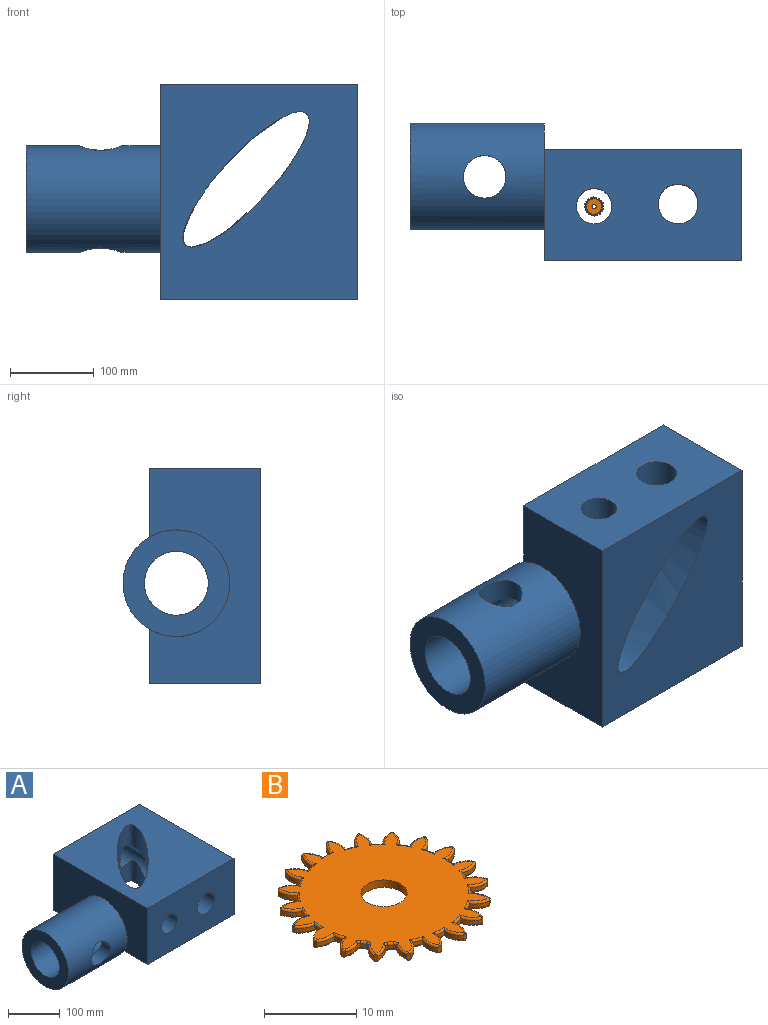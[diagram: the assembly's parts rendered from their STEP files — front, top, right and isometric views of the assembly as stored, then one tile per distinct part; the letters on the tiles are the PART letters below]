
ASSEMBLY  parts=2 mates=1
PART A: 19 faces, bbox 395.5x256.8x164.2 mm
  f0: plane 235.5x116.38mm, normal (0,0,-1), area 22235.5mm2, adj f2,f3,f5,f11,f12,f15,f16
  f1: cylinder r=21.17mm len=150.34mm, axis (0,-1,0), area 14829.1mm2, adj f2,f11,f15
  f2: plane 235.5x132.59mm, normal (0,1,0), area 28054mm2, adj f0,f1,f3,f5,f6,f8
  f3: plane 256.85x132.59mm, normal (-1,0,0), area 23850.9mm2, adj f0,f2,f4,f6,f7,f13
  f4: plane 235.5x132.59mm, normal (0,-1,0), area 28054mm2, adj f3,f5,f6,f7,f8,f10
  f5: plane 256.85x132.59mm, normal (1,0,0), area 29671mm2, adj f0,f2,f4,f6,f7,f16
  f6: plane 256.85x235.5mm, normal (0,0,1), area 50558.2mm2, adj f2,f3,f4,f5,f11
  f7: plane 235.5x98.69mm, normal (0,0,-1), area 21570.9mm2, adj f3,f4,f5,f11,f12,f15,f16
  f8: cylinder r=23.69mm len=256.85mm, axis (0,-1,0), area 26763.2mm2, adj f2,f4,f9,f11,f16
  f9: cylinder r=23.69mm len=12.34mm, axis (0,-1,0), area 49.3mm2, adj f8,f11,f16
  f10: cylinder r=21.17mm len=83.03mm, axis (0,-1,0), area 9437.5mm2, adj f4,f11
  f11: extruded ~161.25x149.84mm, area 41740.2mm2, adj f0,f1,f6,f7,f8,f9,f10,f15
  f12: plane 109.85x31.64mm, normal (1,0,0), area 2287.2mm2, adj f0,f7,f13,f15
  f13: cylinder r=63.5mm len=160.02mm, axis (1,0,0), area 59704.6mm2, adj f3,f12,f14,f17,f18
  f14: plane 127x127mm, normal (-1,0,0), area 8107.3mm2, adj f13,f15
  f15: cylinder r=38.1mm len=235.28mm, axis (-1,0,0), area 42652.1mm2, adj f0,f1,f7,f11,f12,f14,f17,f18
  f16: cylinder r=38.1mm len=157.14mm, axis (-1,0,0), area 18968.1mm2, adj f0,f5,f7,f8,f9,f11
  f17: cylinder r=25.4mm len=50.8mm, axis (0,-1,0), area 4383.1mm2, adj f13,f15
  f18: cylinder r=25.4mm len=50.8mm, axis (0,-1,0), area 4382.4mm2, adj f13,f15
PART B: 214 faces, bbox 23.5x23.5x1 mm
  f0: cylinder r=2.61mm len=2.18mm, axis (0,0,-1), area 1.2mm2, adj f1,f79,f96,f200
  f1: cylinder r=9.41mm len=1.14mm, axis (0,0,-1), area 0.6mm2, adj f0,f2,f95,f201
  f2: cylinder r=2.61mm len=1.71mm, axis (0,0,-1), area 1.2mm2, adj f1,f3,f94,f203
  f3: plane 0.97x0.41mm, normal (-0.38,0.92,0), area 0.4mm2, adj f2,f4,f93,f94,f203,f205
  f4: cylinder r=2.61mm len=2.23mm, axis (0,0,-1), area 1.2mm2, adj f3,f5,f93,f205
  f5: cylinder r=9.41mm len=1mm, axis (0,0,-1), area 0.6mm2, adj f4,f6,f92,f207
  f6: cylinder r=2.61mm len=1.89mm, axis (0,0,-1), area 1.2mm2, adj f5,f7,f91,f209
  f7: plane 0.97x0.34mm, normal (-0.65,0.76,0), area 0.4mm2, adj f6,f8,f90,f91,f209,f211
  f8: cylinder r=2.61mm len=2.06mm, axis (0,0,-1), area 1.2mm2, adj f7,f9,f90,f211
  f9: cylinder r=9.41mm len=0.89mm, axis (0,0,-1), area 0.6mm2, adj f8,f10,f89,f213
  f10: cylinder r=2.61mm len=2.17mm, axis (0,0,-1), area 1.2mm2, adj f9,f11,f88,f212
  f11: plane 0.97x0.38mm, normal (-0.85,0.52,0), area 0.4mm2, adj f10,f12,f87,f88,f210,f212
  f12: cylinder r=2.61mm len=1.68mm, axis (0,0,-1), area 1.2mm2, adj f11,f13,f87,f210
  f13: cylinder r=9.41mm len=1.08mm, axis (0,0,-1), area 0.6mm2, adj f12,f14,f86,f208
  f14: cylinder r=2.61mm len=2.23mm, axis (0,0,-1), area 1.2mm2, adj f13,f15,f85,f206
  f15: plane 0.97x0.43mm, normal (-0.97,0.23,0), area 0.4mm2, adj f14,f16,f84,f85,f204,f206
  f16: cylinder r=2.61mm len=1.92mm, axis (0,0,-1), area 1.2mm2, adj f15,f17,f84,f204
  f17: cylinder r=9.41mm len=1.17mm, axis (0,0,-1), area 0.6mm2, adj f16,f18,f83,f202
  f18: cylinder r=2.61mm len=2.32mm, axis (0,0,-1), area 2.3mm2, adj f17,f19,f81,f82,f83,f169,f202
  f19: plane 0.75x0.44mm, normal (-1,-0.08,0), area 0.3mm2, adj f18,f20,f82,f169,f192
  f20: cylinder r=2.61mm len=2.18mm, axis (0,0,-1), area 1.2mm2, adj f19,f21,f173,f192
  f21: cylinder r=9.41mm len=1.14mm, axis (0,0,-1), area 0.6mm2, adj f20,f22,f176,f195
  f22: cylinder r=2.61mm len=1.71mm, axis (0,0,-1), area 1.2mm2, adj f21,f23,f180,f197
  f23: plane 0.73x0.41mm, normal (-0.92,-0.38,0), area 0.3mm2, adj f22,f24,f183,f197,f198
  f24: cylinder r=2.61mm len=2.02mm, axis (0,0,-1), area 1mm2, adj f23,f186,f193,f198
  f25: cylinder r=9.41mm len=0.59mm, axis (0,0,-1), area 0.3mm2, adj f187,f188,f193,f194
  f26: cylinder r=2.61mm len=1.76mm, axis (0,0,-1), area 1mm2, adj f27,f181,f188,f189
  f27: plane 0.97x0.34mm, normal (-0.76,-0.65,0), area 0.4mm2, adj f26,f28,f177,f181,f185,f189
  f28: cylinder r=2.61mm len=1.89mm, axis (0,0,-1), area 1mm2, adj f27,f177,f178,f185
  f29: cylinder r=9.41mm len=0.52mm, axis (0,0,-1), area 0.3mm2, adj f170,f171,f178,f179
  f30: cylinder r=2.61mm len=1.98mm, axis (0,0,-1), area 1mm2, adj f31,f165,f171,f172
  f31: plane 0.97x0.38mm, normal (-0.52,-0.85,0), area 0.4mm2, adj f30,f32,f163,f165,f168,f172
  f32: cylinder r=2.61mm len=1.68mm, axis (0,0,-1), area 1.2mm2, adj f31,f33,f163,f168
  f33: cylinder r=9.41mm len=1.08mm, axis (0,0,-1), area 0.6mm2, adj f32,f34,f161,f166
  f34: cylinder r=2.61mm len=2.23mm, axis (0,0,-1), area 1.2mm2, adj f33,f35,f159,f164
  f35: plane 0.97x0.43mm, normal (-0.23,-0.97,0), area 0.4mm2, adj f34,f36,f157,f159,f162,f164
  f36: cylinder r=2.61mm len=1.92mm, axis (0,0,-1), area 1.2mm2, adj f35,f37,f157,f162
  f37: cylinder r=9.41mm len=1.17mm, axis (0,0,-1), area 0.6mm2, adj f36,f38,f155,f160
  f38: cylinder r=2.61mm len=2.07mm, axis (0,0,-1), area 1.2mm2, adj f37,f39,f153,f158
  f39: plane 0.97x0.44mm, normal (0.08,-1,0), area 0.4mm2, adj f38,f40,f151,f153,f156,f158
  f40: cylinder r=2.61mm len=2.18mm, axis (0,0,-1), area 1.2mm2, adj f39,f41,f151,f156
  f41: cylinder r=9.41mm len=1.14mm, axis (0,0,-1), area 0.6mm2, adj f40,f42,f149,f154
  f42: cylinder r=2.61mm len=1.71mm, axis (0,0,-1), area 1.2mm2, adj f41,f43,f147,f152
  f43: plane 0.97x0.41mm, normal (0.38,-0.92,0), area 0.4mm2, adj f42,f44,f145,f147,f150,f152
  f44: cylinder r=2.61mm len=2.23mm, axis (0,0,-1), area 1.2mm2, adj f43,f45,f145,f150
  f45: cylinder r=9.41mm len=1mm, axis (0,0,-1), area 0.6mm2, adj f44,f46,f143,f148
  f46: cylinder r=2.61mm len=1.89mm, axis (0,0,-1), area 1.2mm2, adj f45,f47,f141,f146
  f47: plane 0.97x0.34mm, normal (0.65,-0.76,0), area 0.4mm2, adj f46,f48,f139,f141,f144,f146
  f48: cylinder r=2.61mm len=2.06mm, axis (0,0,-1), area 1.2mm2, adj f47,f49,f139,f144
  f49: cylinder r=9.41mm len=0.89mm, axis (0,0,-1), area 0.6mm2, adj f48,f50,f137,f142
  f50: cylinder r=2.61mm len=2.17mm, axis (0,0,-1), area 1.2mm2, adj f49,f51,f135,f140
  f51: plane 0.97x0.38mm, normal (0.85,-0.52,0), area 0.4mm2, adj f50,f52,f133,f135,f138,f140
  f52: cylinder r=2.61mm len=1.68mm, axis (0,0,-1), area 1.2mm2, adj f51,f53,f133,f138
  f53: cylinder r=9.41mm len=1.08mm, axis (0,0,-1), area 0.6mm2, adj f52,f54,f131,f136
  f54: cylinder r=2.61mm len=2.23mm, axis (0,0,-1), area 1.2mm2, adj f53,f55,f129,f134
  f55: plane 0.97x0.43mm, normal (0.97,-0.23,0), area 0.4mm2, adj f54,f56,f127,f129,f132,f134
  f56: cylinder r=2.61mm len=1.92mm, axis (0,0,-1), area 1.2mm2, adj f55,f57,f127,f132
  f57: cylinder r=9.41mm len=1.17mm, axis (0,0,-1), area 0.6mm2, adj f56,f58,f125,f130
  f58: cylinder r=2.61mm len=2.07mm, axis (0,0,-1), area 1.2mm2, adj f57,f59,f123,f128
  f59: plane 0.97x0.44mm, normal (1,0.08,0), area 0.4mm2, adj f58,f60,f121,f123,f126,f128
  f60: cylinder r=2.61mm len=2.18mm, axis (0,0,-1), area 1.2mm2, adj f59,f61,f121,f126
  f61: cylinder r=9.41mm len=1.14mm, axis (0,0,-1), area 0.6mm2, adj f60,f62,f119,f124
  f62: cylinder r=2.61mm len=1.71mm, axis (0,0,-1), area 1.2mm2, adj f61,f63,f117,f122
  f63: plane 0.97x0.41mm, normal (0.92,0.38,0), area 0.4mm2, adj f62,f64,f115,f117,f120,f122
  f64: cylinder r=2.61mm len=2.23mm, axis (0,0,-1), area 1.2mm2, adj f63,f65,f115,f120
  f65: cylinder r=9.41mm len=1mm, axis (0,0,-1), area 0.6mm2, adj f64,f66,f113,f118
  f66: cylinder r=2.61mm len=1.89mm, axis (0,0,-1), area 1.2mm2, adj f65,f67,f111,f116
  f67: plane 0.97x0.34mm, normal (0.76,0.65,0), area 0.4mm2, adj f66,f68,f109,f111,f114,f116
  f68: cylinder r=2.61mm len=2.06mm, axis (0,0,-1), area 1.2mm2, adj f67,f69,f109,f114
  f69: cylinder r=9.41mm len=0.89mm, axis (0,0,-1), area 0.6mm2, adj f68,f70,f107,f112
  f70: cylinder r=2.61mm len=2.17mm, axis (0,0,-1), area 1.2mm2, adj f69,f71,f105,f110
  f71: plane 0.97x0.38mm, normal (0.52,0.85,0), area 0.4mm2, adj f70,f72,f103,f105,f108,f110
  f72: cylinder r=2.61mm len=1.68mm, axis (0,0,-1), area 1.2mm2, adj f71,f73,f103,f108
  f73: cylinder r=9.41mm len=1.08mm, axis (0,0,-1), area 0.6mm2, adj f72,f74,f101,f106
  f74: cylinder r=2.61mm len=2.23mm, axis (0,0,-1), area 1.2mm2, adj f73,f75,f99,f104
  f75: plane 0.97x0.43mm, normal (0.23,0.97,0), area 0.4mm2, adj f74,f76,f97,f99,f102,f104
  f76: cylinder r=2.61mm len=1.92mm, axis (0,0,-1), area 1.2mm2, adj f75,f77,f97,f102
  f77: cylinder r=9.41mm len=1.67mm, axis (0,0,-1), area 0.9mm2, adj f76,f78,f81,f97,f100,f199
  f78: cylinder r=2.61mm len=2.07mm, axis (0,0,-1), area 1.2mm2, adj f77,f79,f98,f199
  f79: plane 0.97x0.44mm, normal (-0.08,1,0), area 0.4mm2, adj f0,f78,f96,f98,f199,f200
  f80: cylinder r=2.5mm len=5mm, axis (0,0,-1), area 15.7mm2, adj f81,f82
  f81: plane 22.67x22.58mm, normal (0,0,1), area 289.9mm2, adj f18,f77,f80,f97,f99,f101,f103,f105
  f82: plane 22.81x22.67mm, normal (0,0,-1), area 289.5mm2, adj f18,f19,f80,f83,f84,f85,f86,f87
  f83: torus R=9.16mm, axis (0,0,1), area 0.5mm2, adj f17,f18,f82,f84
  f84: torus R=2.36mm, axis (0,0,1), area 0.9mm2, adj f15,f16,f82,f83,f85
  f85: torus R=2.36mm, axis (0,0,1), area 0.9mm2, adj f14,f15,f82,f84,f86
  f86: torus R=9.16mm, axis (0,0,1), area 0.5mm2, adj f13,f82,f85,f87
  f87: torus R=2.36mm, axis (0,0,1), area 0.9mm2, adj f11,f12,f82,f86,f88
  f88: torus R=2.36mm, axis (0,0,1), area 0.9mm2, adj f10,f11,f82,f87,f89
  f89: torus R=9.16mm, axis (0,0,1), area 0.5mm2, adj f9,f82,f88,f90
  f90: torus R=2.36mm, axis (0,0,1), area 0.9mm2, adj f7,f8,f82,f89,f91
  f91: torus R=2.36mm, axis (0,0,1), area 0.9mm2, adj f6,f7,f82,f90,f92
  f92: torus R=9.16mm, axis (0,0,1), area 0.5mm2, adj f5,f82,f91,f93
  f93: torus R=2.36mm, axis (0,0,1), area 0.9mm2, adj f3,f4,f82,f92,f94
  f94: torus R=2.36mm, axis (0,0,1), area 0.9mm2, adj f2,f3,f82,f93,f95
  f95: torus R=9.16mm, axis (0,0,1), area 0.5mm2, adj f1,f82,f94,f96
  f96: torus R=2.36mm, axis (0,0,1), area 0.9mm2, adj f0,f79,f82,f95,f98
  f97: torus R=2.36mm, axis (0,0,1), area 0.9mm2, adj f75,f76,f77,f81,f99
  f98: torus R=2.36mm, axis (0,0,1), area 0.9mm2, adj f78,f79,f82,f96,f100
  f99: torus R=2.36mm, axis (0,0,1), area 0.9mm2, adj f74,f75,f81,f97,f101
  f100: torus R=9.16mm, axis (0,0,1), area 0.5mm2, adj f77,f82,f98,f102
  f101: torus R=9.16mm, axis (0,0,1), area 0.5mm2, adj f73,f81,f99,f103
  f102: torus R=2.36mm, axis (0,0,1), area 0.9mm2, adj f75,f76,f82,f100,f104
  f103: torus R=2.36mm, axis (0,0,1), area 0.9mm2, adj f71,f72,f81,f101,f105
  f104: torus R=2.36mm, axis (0,0,1), area 0.9mm2, adj f74,f75,f82,f102,f106
  f105: torus R=2.36mm, axis (0,0,1), area 0.9mm2, adj f70,f71,f81,f103,f107
  f106: torus R=9.16mm, axis (0,0,1), area 0.5mm2, adj f73,f82,f104,f108
  f107: torus R=9.16mm, axis (0,0,1), area 0.5mm2, adj f69,f81,f105,f109
  f108: torus R=2.36mm, axis (0,0,1), area 0.9mm2, adj f71,f72,f82,f106,f110
  f109: torus R=2.36mm, axis (0,0,1), area 0.9mm2, adj f67,f68,f81,f107,f111
  f110: torus R=2.36mm, axis (0,0,1), area 0.9mm2, adj f70,f71,f82,f108,f112
  f111: torus R=2.36mm, axis (0,0,1), area 0.9mm2, adj f66,f67,f81,f109,f113
  f112: torus R=9.16mm, axis (0,0,1), area 0.5mm2, adj f69,f82,f110,f114
  f113: torus R=9.16mm, axis (0,0,1), area 0.5mm2, adj f65,f81,f111,f115
  f114: torus R=2.36mm, axis (0,0,1), area 0.9mm2, adj f67,f68,f82,f112,f116
  f115: torus R=2.36mm, axis (0,0,1), area 0.9mm2, adj f63,f64,f81,f113,f117
  f116: torus R=2.36mm, axis (0,0,1), area 0.9mm2, adj f66,f67,f82,f114,f118
  f117: torus R=2.36mm, axis (0,0,1), area 0.9mm2, adj f62,f63,f81,f115,f119
  f118: torus R=9.16mm, axis (0,0,1), area 0.5mm2, adj f65,f82,f116,f120
  f119: torus R=9.16mm, axis (0,0,1), area 0.5mm2, adj f61,f81,f117,f121
  f120: torus R=2.36mm, axis (0,0,1), area 0.9mm2, adj f63,f64,f82,f118,f122
  f121: torus R=2.36mm, axis (0,0,1), area 0.9mm2, adj f59,f60,f81,f119,f123
  f122: torus R=2.36mm, axis (0,0,1), area 0.9mm2, adj f62,f63,f82,f120,f124
  f123: torus R=2.36mm, axis (0,0,1), area 0.9mm2, adj f58,f59,f81,f121,f125
  f124: torus R=9.16mm, axis (0,0,1), area 0.5mm2, adj f61,f82,f122,f126
  f125: torus R=9.16mm, axis (0,0,1), area 0.5mm2, adj f57,f81,f123,f127
  f126: torus R=2.36mm, axis (0,0,1), area 0.9mm2, adj f59,f60,f82,f124,f128
  f127: torus R=2.36mm, axis (0,0,1), area 0.9mm2, adj f55,f56,f81,f125,f129
  f128: torus R=2.36mm, axis (0,0,1), area 0.9mm2, adj f58,f59,f82,f126,f130
  f129: torus R=2.36mm, axis (0,0,1), area 0.9mm2, adj f54,f55,f81,f127,f131
  f130: torus R=9.16mm, axis (0,0,1), area 0.5mm2, adj f57,f82,f128,f132
  f131: torus R=9.16mm, axis (0,0,1), area 0.5mm2, adj f53,f81,f129,f133
  f132: torus R=2.36mm, axis (0,0,1), area 0.9mm2, adj f55,f56,f82,f130,f134
  f133: torus R=2.36mm, axis (0,0,1), area 0.9mm2, adj f51,f52,f81,f131,f135
  f134: torus R=2.36mm, axis (0,0,1), area 0.9mm2, adj f54,f55,f82,f132,f136
  f135: torus R=2.36mm, axis (0,0,1), area 0.9mm2, adj f50,f51,f81,f133,f137
  f136: torus R=9.16mm, axis (0,0,1), area 0.5mm2, adj f53,f82,f134,f138
  f137: torus R=9.16mm, axis (0,0,1), area 0.5mm2, adj f49,f81,f135,f139
  f138: torus R=2.36mm, axis (0,0,1), area 0.9mm2, adj f51,f52,f82,f136,f140
  f139: torus R=2.36mm, axis (0,0,1), area 0.9mm2, adj f47,f48,f81,f137,f141
  f140: torus R=2.36mm, axis (0,0,1), area 0.9mm2, adj f50,f51,f82,f138,f142
  f141: torus R=2.36mm, axis (0,0,1), area 0.9mm2, adj f46,f47,f81,f139,f143
  f142: torus R=9.16mm, axis (0,0,1), area 0.5mm2, adj f49,f82,f140,f144
  f143: torus R=9.16mm, axis (0,0,1), area 0.5mm2, adj f45,f81,f141,f145
  f144: torus R=2.36mm, axis (0,0,1), area 0.9mm2, adj f47,f48,f82,f142,f146
  f145: torus R=2.36mm, axis (0,0,1), area 0.9mm2, adj f43,f44,f81,f143,f147
  f146: torus R=2.36mm, axis (0,0,1), area 0.9mm2, adj f46,f47,f82,f144,f148
  f147: torus R=2.36mm, axis (0,0,1), area 0.9mm2, adj f42,f43,f81,f145,f149
  f148: torus R=9.16mm, axis (0,0,1), area 0.5mm2, adj f45,f82,f146,f150
  f149: torus R=9.16mm, axis (0,0,1), area 0.5mm2, adj f41,f81,f147,f151
  f150: torus R=2.36mm, axis (0,0,1), area 0.9mm2, adj f43,f44,f82,f148,f152
  f151: torus R=2.36mm, axis (0,0,1), area 0.9mm2, adj f39,f40,f81,f149,f153
  f152: torus R=2.36mm, axis (0,0,1), area 0.9mm2, adj f42,f43,f82,f150,f154
  f153: torus R=2.36mm, axis (0,0,1), area 0.9mm2, adj f38,f39,f81,f151,f155
  f154: torus R=9.16mm, axis (0,0,1), area 0.5mm2, adj f41,f82,f152,f156
  f155: torus R=9.16mm, axis (0,0,1), area 0.5mm2, adj f37,f81,f153,f157
  f156: torus R=2.36mm, axis (0,0,1), area 0.9mm2, adj f39,f40,f82,f154,f158
  f157: torus R=2.36mm, axis (0,0,1), area 0.9mm2, adj f35,f36,f81,f155,f159
  f158: torus R=2.36mm, axis (0,0,1), area 0.9mm2, adj f38,f39,f82,f156,f160
  f159: torus R=2.36mm, axis (0,0,1), area 0.9mm2, adj f34,f35,f81,f157,f161
  f160: torus R=9.16mm, axis (0,0,1), area 0.5mm2, adj f37,f82,f158,f162
  f161: torus R=9.16mm, axis (0,0,1), area 0.5mm2, adj f33,f81,f159,f163
  f162: torus R=2.36mm, axis (0,0,1), area 0.9mm2, adj f35,f36,f82,f160,f164
  f163: torus R=2.36mm, axis (0,0,1), area 0.9mm2, adj f31,f32,f81,f161,f165
  f164: torus R=2.36mm, axis (0,0,1), area 0.9mm2, adj f34,f35,f82,f162,f166
  f165: torus R=2.36mm, axis (0,0,1), area 0.8mm2, adj f30,f31,f81,f163,f167
  f166: torus R=9.16mm, axis (0,0,1), area 0.5mm2, adj f33,f82,f164,f168
  f167: torus R=0.5mm, axis (0,0,1), area 0.2mm2, adj f81,f165,f170,f171
  f168: torus R=2.36mm, axis (0,0,1), area 0.9mm2, adj f31,f32,f82,f166,f172
  f169: cylinder r=0.25mm len=0.66mm, axis (-0.08,1,0), area 0.2mm2, adj f18,f19,f81,f173
  f170: torus R=9.16mm, axis (0,0,1), area 0.3mm2, adj f29,f81,f167,f174
  f171: cylinder r=0.25mm len=0.5mm, axis (0,0,1), area 0.2mm2, adj f29,f30,f167,f175
  f172: torus R=2.36mm, axis (0,0,1), area 0.8mm2, adj f30,f31,f82,f168,f175
  f173: torus R=2.36mm, axis (0,0,1), area 0.9mm2, adj f20,f81,f169,f176
  f174: torus R=0.5mm, axis (0,0,1), area 0.2mm2, adj f81,f170,f177,f178
  f175: torus R=0.5mm, axis (0,0,1), area 0.2mm2, adj f82,f171,f172,f179
  f176: torus R=9.16mm, axis (0,0,1), area 0.5mm2, adj f21,f81,f173,f180
  f177: torus R=2.36mm, axis (0,0,1), area 0.8mm2, adj f27,f28,f81,f174,f181
  f178: cylinder r=0.25mm len=0.5mm, axis (0,0,1), area 0.2mm2, adj f28,f29,f174,f182
  f179: torus R=9.16mm, axis (0,0,1), area 0.3mm2, adj f29,f82,f175,f182
  f180: torus R=2.36mm, axis (0,0,1), area 0.9mm2, adj f22,f81,f176,f183
  f181: torus R=2.36mm, axis (0,0,1), area 0.8mm2, adj f26,f27,f81,f177,f184
  f182: torus R=0.5mm, axis (0,0,1), area 0.2mm2, adj f82,f178,f179,f185
  f183: cylinder r=0.25mm len=0.5mm, axis (-0.38,0.92,0), area 0.1mm2, adj f23,f81,f180,f186
  f184: torus R=0.5mm, axis (0,0,1), area 0.2mm2, adj f81,f181,f187,f188
  f185: torus R=2.36mm, axis (0,0,1), area 0.8mm2, adj f27,f28,f82,f182,f189
  f186: torus R=2.36mm, axis (0,0,1), area 0.8mm2, adj f24,f81,f183,f190
  f187: torus R=9.16mm, axis (0,0,1), area 0.3mm2, adj f25,f81,f184,f190
  f188: cylinder r=0.25mm len=0.5mm, axis (0,0,1), area 0.2mm2, adj f25,f26,f184,f191
  f189: torus R=2.36mm, axis (0,0,1), area 0.8mm2, adj f26,f27,f82,f185,f191
  f190: torus R=0.5mm, axis (0,0,1), area 0.2mm2, adj f81,f186,f187,f193
  f191: torus R=0.5mm, axis (0,0,1), area 0.2mm2, adj f82,f188,f189,f194
  f192: torus R=2.36mm, axis (0,0,1), area 0.9mm2, adj f19,f20,f82,f195
  f193: cylinder r=0.25mm len=0.5mm, axis (0,0,1), area 0.2mm2, adj f24,f25,f190,f196
  f194: torus R=9.16mm, axis (0,0,1), area 0.3mm2, adj f25,f82,f191,f196
  f195: torus R=9.16mm, axis (0,0,1), area 0.5mm2, adj f21,f82,f192,f197
  f196: torus R=0.5mm, axis (0,0,1), area 0.2mm2, adj f82,f193,f194,f198
  f197: torus R=2.36mm, axis (0,0,1), area 0.9mm2, adj f22,f23,f82,f195,f198
  f198: torus R=2.36mm, axis (0,0,1), area 0.8mm2, adj f23,f24,f82,f196,f197
  f199: torus R=2.36mm, axis (0,0,1), area 0.9mm2, adj f77,f78,f79,f81,f200
  f200: torus R=2.36mm, axis (0,0,1), area 0.9mm2, adj f0,f79,f81,f199,f201
  f201: torus R=9.16mm, axis (0,0,1), area 0.5mm2, adj f1,f81,f200,f203
  f202: torus R=9.16mm, axis (0,0,1), area 0.5mm2, adj f17,f18,f81,f204
  f203: torus R=2.36mm, axis (0,0,1), area 0.9mm2, adj f2,f3,f81,f201,f205
  f204: torus R=2.36mm, axis (0,0,1), area 0.9mm2, adj f15,f16,f81,f202,f206
  f205: torus R=2.36mm, axis (0,0,1), area 0.9mm2, adj f3,f4,f81,f203,f207
  f206: torus R=2.36mm, axis (0,0,1), area 0.9mm2, adj f14,f15,f81,f204,f208
  f207: torus R=9.16mm, axis (0,0,1), area 0.5mm2, adj f5,f81,f205,f209
  f208: torus R=9.16mm, axis (0,0,1), area 0.5mm2, adj f13,f81,f206,f210
  f209: torus R=2.36mm, axis (0,0,1), area 0.9mm2, adj f6,f7,f81,f207,f211
  f210: torus R=2.36mm, axis (0,0,1), area 0.9mm2, adj f11,f12,f81,f208,f212
  f211: torus R=2.36mm, axis (0,0,1), area 0.9mm2, adj f7,f8,f81,f209,f213
  f212: torus R=2.36mm, axis (0,0,1), area 0.9mm2, adj f10,f11,f81,f210,f213
  f213: torus R=9.16mm, axis (0,0,1), area 0.5mm2, adj f9,f81,f211,f212
PLACE A rot(axis=(1,0,0),90deg) t=(-133.34,132.59,14.69)mm
PLACE B rot(axis=(0,0,1),125.1deg) t=(-176.21,64.87,-128.92)mm
MATE revolute A.f1 <-> B.f1  axis (0,0,-1) through (-176.21,64.87,-128.42)mm
